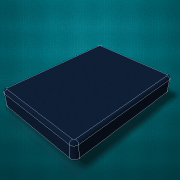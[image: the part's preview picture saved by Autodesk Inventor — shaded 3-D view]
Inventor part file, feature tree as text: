
AUTODESK INVENTOR PART (.ipt)
format: ipt  version: 2017 (Build 210142000, 142)  size: 158,720 bytes
history: native  units: in
note: dims shown in document units (in); Inventor stores cm internally (conversion verified against a paired STEP export)
features: fillet x3, extrude x1, sketch x1
ambient origin geometry x8: Origin, YZ Plane, XZ Plane, XY Plane, X Axis, Y Axis, Z Axis, Center Point
bodies: Solid1 (feature_tree)
feature tree (5):
  extrude  "Extrusion1"  Depth=80.0in
  fillet  "Fillet1"  Radius=12.0in
  fillet  "Fillet2"  Radius=3.0in
  fillet  "Fillet3"  Radius=2.0in
  sketch  "Sketch1"  dims[d0=60.0in d1=80.0in d2=12.0in d3=0.0in d4=3.0in d5=2.0in d6=1.0in]
